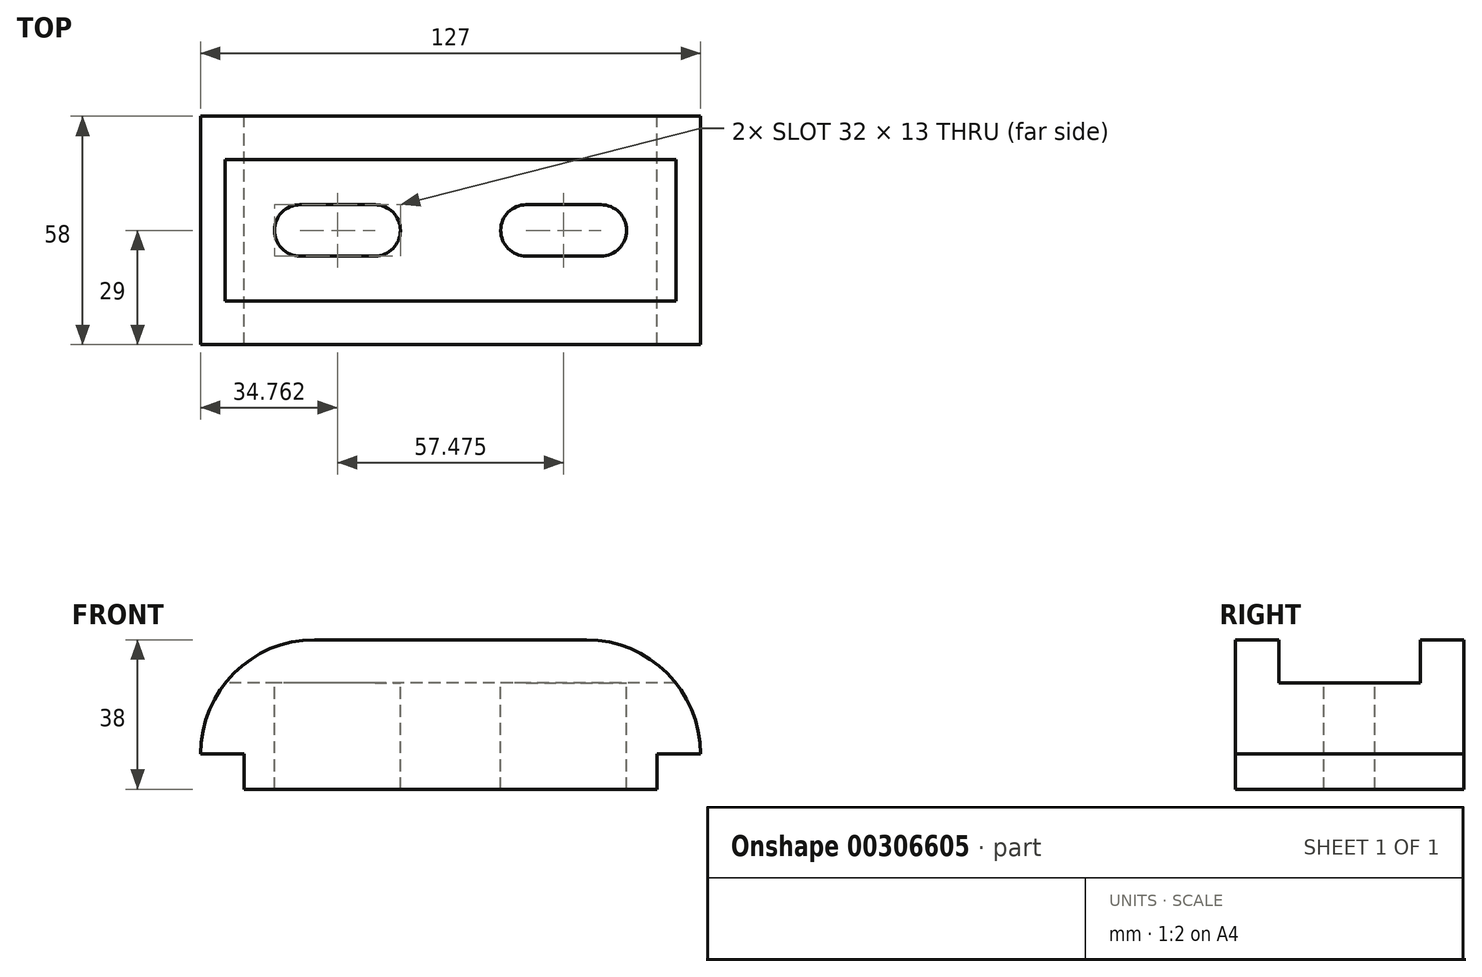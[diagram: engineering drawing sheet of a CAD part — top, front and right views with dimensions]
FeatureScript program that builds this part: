
annotation { "Feature Type Name" : "Feature", "Feature Type Description" : "" }
export const myFeature = defineFeature(function(context is Context, id is Id, definition is map)
    precondition{}
    {
        {
            var Q0;
            Q0=qCreatedBy(makeId("Front.planeOp"),FACE);
            var sketch = newSketch(context, id + "F0", { "sketchPlane" : qUnion([Q0])});
            skLineSegment(sketch, "E0", {"start": v(0, 0) * mm, "end": v(105, 0) * mm});
            skLineSegment(sketch, "E1", {"start": v(105, 0) * mm, "end": v(105, 9) * mm});
            skLineSegment(sketch, "E2", {"start": v(105, 9) * mm, "end": v(116, 9) * mm});
            skLineSegment(sketch, "E3", {"start": v(116, 9) * mm, "end": v(116, 38) * mm});
            skLineSegment(sketch, "E4", {"start": v(116, 38) * mm, "end": v(-11, 38) * mm});
            skLineSegment(sketch, "E5", {"start": v(-11, 38) * mm, "end": v(-11, 9) * mm});
            skLineSegment(sketch, "E6", {"start": v(-11, 9) * mm, "end": v(0, 9) * mm});
            skLineSegment(sketch, "E7", {"start": v(0, 9) * mm, "end": v(0, 0) * mm});
            skSolve(sketch);
        }
        {
            var Q0;
            Q0 = qSketchRegion(id + "F0", true);
            extrude(context, id + "F1", {"entities" : qUnion([Q0]), "depth" : 58 * mm});
        }
        {
            var Q0;
            Q0=makeQuery(id+"F1.opExtrude","SWEPT_FACE",FACE,{"disambiguationData":[OSD([sQuery(id+"F0.wireOp",EDGE,"E5")])]});
            var sketch = newSketch(context, id + "F2", { "sketchPlane" : qUnion([Q0])});
            skLineSegment(sketch, "E8", {"start": v(0, 38) * mm, "end": v(11, 38) * mm});
            skLineSegment(sketch, "E9", {"start": v(58, 38) * mm, "end": v(47, 38) * mm});
            skLineSegment(sketch, "E10", {"start": v(47, 38) * mm, "end": v(11, 38) * mm});
            skLineSegment(sketch, "E11", {"start": v(11, 27) * mm, "end": v(11, 38) * mm});
            skLineSegment(sketch, "E12", {"start": v(47, 27) * mm, "end": v(11, 27) * mm});
            skLineSegment(sketch, "E13", {"start": v(47, 38) * mm, "end": v(47, 27) * mm});
            skSolve(sketch);
        }
        {
            var Q0;
            Q0 = qSketchRegion(id + "F2", true);
            extrude(context, id + "F3", {"entities" : qUnion([Q0]), "operationType" : NewBodyOperationType.REMOVE, "oppositeDirection" : true, "depth" : 128 * mm});
        }
        {
            var Q0;
            {var subQ0=sQuery(id+"F0.wireOp",EDGE,"E5");var subQ1=sQuery(id+"F0.wireOp",EDGE,"E4");Q0=makeQuery(id+"F3.boolean.opBoolean","SPLIT",EDGE,{"disambiguationData":[TD([makeQuery(id+"F3.opExtrude","SWEPT_FACE",FACE,{"disambiguationData":[OSD([sQuery(id+"F2.wireOp",EDGE,"E11")])]})])],"derivedFrom":makeQuery(id+"F1.opExtrude","SWEPT_EDGE",EDGE,{"disambiguationData":[OSD([subQ1,subQ0])]})});}
            var Q1;
            {var subQ0=sQuery(id+"F0.wireOp",EDGE,"E4");var subQ1=sQuery(id+"F0.wireOp",EDGE,"E3");Q1=makeQuery(id+"F3.boolean.opBoolean","SPLIT",EDGE,{"disambiguationData":[TD([makeQuery(id+"F3.opExtrude","SWEPT_FACE",FACE,{"disambiguationData":[OSD([sQuery(id+"F2.wireOp",EDGE,"E13")])]})])],"derivedFrom":makeQuery(id+"F1.opExtrude","SWEPT_EDGE",EDGE,{"disambiguationData":[OSD([subQ1,subQ0])]})});}
            fillet(context, id + "F4", {"entities" : qUnion([Q0, Q1]), "radius" : 29 * mm, "tangentPropagation" : true, "allowEdgeOverflow" : false});
        }
        {
            var Q0;
            Q0=makeQuery(id+"F3.boolean.opBoolean","COPY",FACE,{"derivedFrom":makeQuery(id+"F3.opExtrude","SWEPT_FACE",FACE,{"disambiguationData":[OSD([sQuery(id+"F2.wireOp",EDGE,"E12")])]})});
            var sketch = newSketch(context, id + "F5", { "sketchPlane" : qUnion([Q0])});
            skArc(sketch, "E14", {"start": v(90.74, -35.5) * mm, "mid": v(97.24, -29) * mm, "end": v(90.74, -22.5) * mm});
            skArc(sketch, "E15", {"start": v(71.74, -22.5) * mm, "mid": v(65.24, -29) * mm, "end": v(71.74, -35.5) * mm});
            skArc(sketch, "E16", {"start": v(33.26, -35.5) * mm, "mid": v(39.76, -29) * mm, "end": v(33.26, -22.5) * mm});
            skArc(sketch, "E17", {"start": v(14.26, -22.5) * mm, "mid": v(7.76, -29) * mm, "end": v(14.26, -35.5) * mm});
            skLineSegment(sketch, "E18", {"start": v(14.26, -35.5) * mm, "end": v(33.26, -35.5) * mm});
            skLineSegment(sketch, "E19", {"start": v(33.26, -22.5) * mm, "end": v(14.26, -22.5) * mm});
            skLineSegment(sketch, "E20", {"start": v(71.74, -22.5) * mm, "end": v(90.74, -22.5) * mm});
            skLineSegment(sketch, "E21", {"start": v(90.74, -35.5) * mm, "end": v(71.74, -35.5) * mm});
            skSolve(sketch);
        }
        {
            var Q0;
            Q0 = qSketchRegion(id + "F5", true);
            extrude(context, id + "F6", {"entities" : qUnion([Q0]), "operationType" : NewBodyOperationType.REMOVE, "oppositeDirection" : true, "depth" : 100 * mm});
        }
    });
